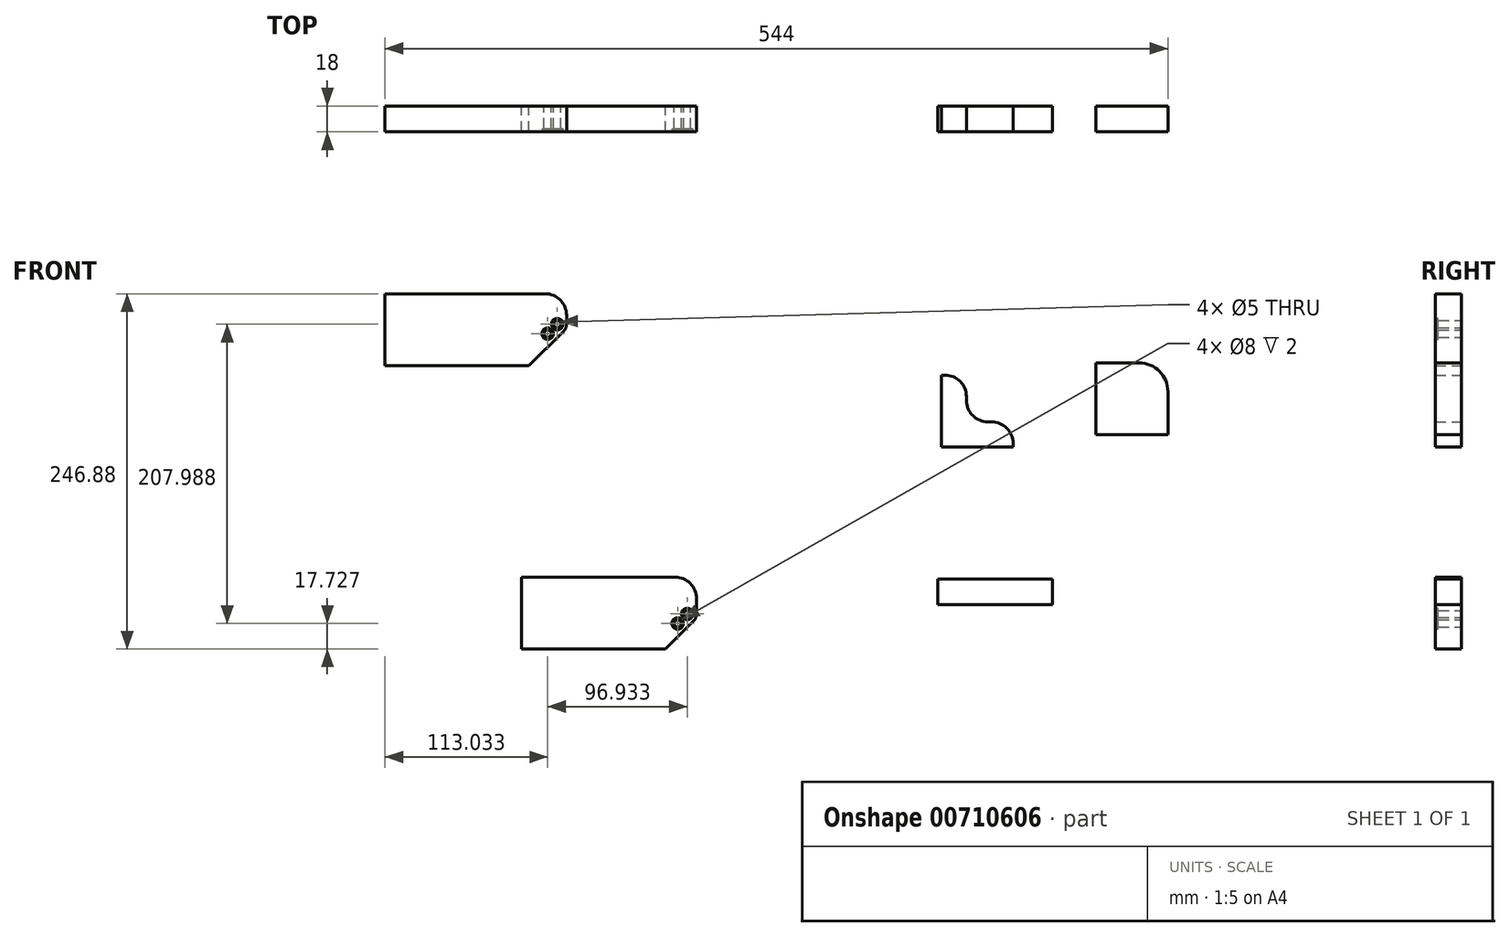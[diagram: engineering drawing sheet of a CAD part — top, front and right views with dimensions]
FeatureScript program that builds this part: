
annotation { "Feature Type Name" : "Feature", "Feature Type Description" : "" }
export const myFeature = defineFeature(function(context is Context, id is Id, definition is map)
    precondition{}
    {
        {
            var Q0;
            Q0=qCreatedBy(makeId("Front.planeOp"),FACE);
            var sketch = newSketch(context, id + "F0", { "sketchPlane" : qUnion([Q0])});
            skLineSegment(sketch, "E0", {"start": v(0, 0) * mm, "end": v(100, 0) * mm});
            skLineSegment(sketch, "E1", {"start": v(100, 0) * mm, "end": v(119.74, 19.74) * mm});
            skLineSegment(sketch, "E2", {"start": v(121.65, 24.34) * mm, "end": v(121.65, 35) * mm});
            skLineSegment(sketch, "E3", {"start": v(106.65, 50) * mm, "end": v(0, 50) * mm});
            skLineSegment(sketch, "E4", {"start": v(0, 50) * mm, "end": v(0, 0) * mm});
            skCircle(sketch, "E5", {"center": v(108.53, 17.73) * mm, "radius": 4 * mm, "construction": true});
            skCircle(sketch, "E6", {"center": v(115.15, 24.34) * mm, "radius": 4 * mm, "construction": true});
            skCircle(sketch, "E7", {"center": v(108.53, 17.73) * mm, "radius": 2.5 * mm});
            skCircle(sketch, "E8", {"center": v(115.15, 24.34) * mm, "radius": 2.5 * mm});
            skLineSegment(sketch, "E9", {"start": v(108.53, 17.73) * mm, "end": v(115.15, 24.34) * mm, "construction": true});
            skLineSegment(sketch, "E10", {"start": v(97.22, 34.7) * mm, "end": v(167.93, -36.01) * mm, "construction": true});
            skLineSegment(sketch, "E11", {"start": v(167.93, -36.01) * mm, "end": v(168.89, -35.06) * mm, "construction": true});
            skLineSegment(sketch, "E12", {"start": v(168.89, -35.06) * mm, "end": v(98.18, 35.65) * mm, "construction": true});
            skLineSegment(sketch, "E13", {"start": v(98.18, 35.65) * mm, "end": v(97.22, 34.7) * mm, "construction": true});
            skLineSegment(sketch, "E14", {"start": v(122.83, 20) * mm, "end": v(122.83, 2) * mm, "construction": true});
            skLineSegment(sketch, "E15", {"start": v(122.83, 2) * mm, "end": v(166.06, 2) * mm, "construction": true});
            skLineSegment(sketch, "E16", {"start": v(166.06, 2) * mm, "end": v(166.06, 20) * mm, "construction": true});
            skLineSegment(sketch, "E17", {"start": v(166.06, 20) * mm, "end": v(122.83, 20) * mm, "construction": true});
            skPoint(sketch, "E18", {"position": v(122.83, 11) * mm});
            skLineSegment(sketch, "E19", {"start": v(143.18, -11.26) * mm, "end": v(144.14, -10.3) * mm, "construction": true});
            skLineSegment(sketch, "E20", {"start": v(0, 0) * mm, "end": v(0, -18) * mm, "construction": true});
            skLineSegment(sketch, "E21", {"start": v(0, -18) * mm, "end": v(233.18, -18) * mm, "construction": true});
            skLineSegment(sketch, "E22", {"start": v(233.18, -18) * mm, "end": v(233.18, 0) * mm, "construction": true});
            skLineSegment(sketch, "E23", {"start": v(233.18, 0) * mm, "end": v(100, 0) * mm, "construction": true});
            skLineSegment(sketch, "E24", {"start": v(289.16, 30.72) * mm, "end": v(344.25, 30.72) * mm});
            skLineSegment(sketch, "E25", {"start": v(344.25, 30.72) * mm, "end": v(344.25, 85.54) * mm});
            skLineSegment(sketch, "E26", {"start": v(344.25, 30.72) * mm, "end": v(298.29, 76.69) * mm});
            skLineSegment(sketch, "E27", {"start": v(289.16, 30.72) * mm, "end": v(289.16, 48.72) * mm});
            skLineSegment(sketch, "E28", {"start": v(289.16, 48.72) * mm, "end": v(369.01, 48.72) * mm});
            skLineSegment(sketch, "E29", {"start": v(369.01, 48.72) * mm, "end": v(369.01, 30.72) * mm});
            skLineSegment(sketch, "E30", {"start": v(369.01, 30.72) * mm, "end": v(344.25, 30.72) * mm});
            skLineSegment(sketch, "E31", {"start": v(-94.82, 196.88) * mm, "end": v(5.18, 196.88) * mm});
            skLineSegment(sketch, "E32", {"start": v(5.18, 196.88) * mm, "end": v(29.42, 221.12) * mm});
            skLineSegment(sketch, "E33", {"start": v(31.32, 225.72) * mm, "end": v(31.32, 231.88) * mm});
            skLineSegment(sketch, "E34", {"start": v(16.32, 246.88) * mm, "end": v(-94.82, 246.88) * mm});
            skLineSegment(sketch, "E35", {"start": v(-94.82, 246.88) * mm, "end": v(-94.82, 196.88) * mm});
            skCircle(sketch, "E36", {"center": v(18.21, 219.1) * mm, "radius": 4 * mm, "construction": true});
            skCircle(sketch, "E37", {"center": v(24.82, 225.72) * mm, "radius": 4 * mm, "construction": true});
            skCircle(sketch, "E38", {"center": v(18.21, 219.1) * mm, "radius": 2.5 * mm});
            skCircle(sketch, "E39", {"center": v(24.82, 225.72) * mm, "radius": 2.5 * mm});
            skLineSegment(sketch, "E40", {"start": v(18.21, 219.1) * mm, "end": v(24.82, 225.72) * mm, "construction": true});
            skLineSegment(sketch, "E41", {"start": v(6.9, 236.07) * mm, "end": v(77.61, 165.36) * mm, "construction": true});
            skLineSegment(sketch, "E42", {"start": v(77.61, 165.36) * mm, "end": v(78.56, 166.32) * mm, "construction": true});
            skLineSegment(sketch, "E43", {"start": v(78.56, 166.32) * mm, "end": v(7.85, 237.03) * mm, "construction": true});
            skLineSegment(sketch, "E44", {"start": v(7.85, 237.03) * mm, "end": v(6.9, 236.07) * mm, "construction": true});
            skLineSegment(sketch, "E45", {"start": v(28, 216.88) * mm, "end": v(28, 198.88) * mm, "construction": true});
            skLineSegment(sketch, "E46", {"start": v(28, 198.88) * mm, "end": v(71.24, 198.88) * mm, "construction": true});
            skLineSegment(sketch, "E47", {"start": v(71.24, 198.88) * mm, "end": v(71.24, 216.88) * mm, "construction": true});
            skLineSegment(sketch, "E48", {"start": v(71.24, 216.88) * mm, "end": v(28, 216.88) * mm, "construction": true});
            skPoint(sketch, "E49", {"position": v(28, 207.88) * mm});
            skLineSegment(sketch, "E50", {"start": v(52.86, 190.11) * mm, "end": v(53.82, 191.07) * mm, "construction": true});
            skLineSegment(sketch, "E51", {"start": v(-94.82, 196.88) * mm, "end": v(-94.82, 178.88) * mm, "construction": true});
            skLineSegment(sketch, "E52", {"start": v(-94.82, 178.88) * mm, "end": v(156.01, 178.88) * mm, "construction": true});
            skLineSegment(sketch, "E53", {"start": v(156.01, 178.88) * mm, "end": v(156.01, 196.88) * mm, "construction": true});
            skLineSegment(sketch, "E54", {"start": v(156.01, 196.88) * mm, "end": v(5.18, 196.88) * mm, "construction": true});
            skPoint(sketch, "E55.visualSharp", {"position": v(31.32, 223.02) * mm});
            skArc(sketch, "E55.filletArc", {"start": v(29.42, 221.12) * mm, "mid": v(30.83, 223.23) * mm, "end": v(31.32, 225.72) * mm});
            skPoint(sketch, "E56.visualSharp", {"position": v(121.65, 21.65) * mm});
            skArc(sketch, "E56.filletArc", {"start": v(119.74, 19.74) * mm, "mid": v(121.15, 21.85) * mm, "end": v(121.65, 24.34) * mm});
            skPoint(sketch, "E57.visualSharp", {"position": v(31.32, 246.88) * mm});
            skArc(sketch, "E57.filletArc", {"start": v(31.32, 231.88) * mm, "mid": v(26.93, 242.48) * mm, "end": v(16.32, 246.88) * mm});
            skPoint(sketch, "E58.visualSharp", {"position": v(121.65, 50) * mm});
            skArc(sketch, "E58.filletArc", {"start": v(121.65, 35) * mm, "mid": v(117.25, 45.6) * mm, "end": v(106.65, 50) * mm});
            skLineSegment(sketch, "E59.bottom", {"start": v(291.67, 140.34) * mm, "end": v(341.67, 140.34) * mm});
            skLineSegment(sketch, "E59.top", {"start": v(291.67, 190.34) * mm, "end": v(294.17, 190.34) * mm});
            skLineSegment(sketch, "E59.left", {"start": v(291.67, 140.34) * mm, "end": v(291.67, 190.34) * mm});
            skLineSegment(sketch, "E59.right", {"start": v(341.67, 140.34) * mm, "end": v(341.67, 142.84) * mm});
            skLineSegment(sketch, "E60.top", {"start": v(326.67, 157.84) * mm, "end": v(324.17, 157.84) * mm});
            skLineSegment(sketch, "E60.right", {"start": v(309.17, 175.34) * mm, "end": v(309.17, 172.84) * mm});
            skPoint(sketch, "E61.visualSharp", {"position": v(309.17, 190.34) * mm});
            skArc(sketch, "E61.filletArc", {"start": v(309.17, 175.34) * mm, "mid": v(304.77, 185.94) * mm, "end": v(294.17, 190.34) * mm});
            skPoint(sketch, "E62.visualSharp", {"position": v(309.17, 157.84) * mm});
            skArc(sketch, "E62.filletArc", {"start": v(309.17, 172.84) * mm, "mid": v(313.56, 162.23) * mm, "end": v(324.17, 157.84) * mm});
            skPoint(sketch, "E63.visualSharp", {"position": v(341.67, 157.84) * mm});
            skArc(sketch, "E63.filletArc", {"start": v(341.67, 142.84) * mm, "mid": v(337.27, 153.44) * mm, "end": v(326.67, 157.84) * mm});
            skLineSegment(sketch, "E64.bottom", {"start": v(399.18, 148.83) * mm, "end": v(449.18, 148.83) * mm});
            skLineSegment(sketch, "E64.top", {"start": v(399.18, 198.83) * mm, "end": v(429.18, 198.83) * mm});
            skLineSegment(sketch, "E64.left", {"start": v(399.18, 148.83) * mm, "end": v(399.18, 198.83) * mm});
            skLineSegment(sketch, "E64.right", {"start": v(449.18, 148.83) * mm, "end": v(449.18, 178.83) * mm});
            skPoint(sketch, "E65.visualSharp", {"position": v(449.18, 198.83) * mm});
            skArc(sketch, "E65.filletArc", {"start": v(449.18, 178.83) * mm, "mid": v(443.32, 192.97) * mm, "end": v(429.18, 198.83) * mm});
            skSolve(sketch);
        }
        {
            var Q0;
            Q0 = qSketchRegion(id + "F0", true);
            extrude(context, id + "F1", {"entities" : qUnion([Q0]), "depth" : 18 * mm, "offsetDistance" : 25 * mm});
        }
        {
            var Q0;
            Q0=makeQuery(id+"F1.opExtrude","CAP_FACE",FACE,{"disambiguationData":[OSD([sQuery(id+"F0.wireOp",EDGE,"E31"),sQuery(id+"F0.wireOp",EDGE,"E32"),sQuery(id+"F0.wireOp",EDGE,"E33"),sQuery(id+"F0.wireOp",EDGE,"E34"),sQuery(id+"F0.wireOp",EDGE,"E35"),sQuery(id+"F0.wireOp",EDGE,"E38"),sQuery(id+"F0.wireOp",EDGE,"E39"),sQuery(id+"F0.wireOp",EDGE,"E55.filletArc"),sQuery(id+"F0.wireOp",EDGE,"E57.filletArc")])],"isStart":false});
            var sketch = newSketch(context, id + "F2", { "sketchPlane" : qUnion([Q0])});
            skCircle(sketch, "E66", {"center": v(18.21, 219.1) * mm, "radius": 4 * mm});
            skCircle(sketch, "E67", {"center": v(24.82, 225.72) * mm, "radius": 4 * mm});
            skCircle(sketch, "E68", {"center": v(115.15, 24.34) * mm, "radius": 4 * mm});
            skCircle(sketch, "E69", {"center": v(108.53, 17.73) * mm, "radius": 4 * mm});
            skSolve(sketch);
        }
        {
            var Q0;
            Q0 = qSketchRegion(id + "F2", true);
            extrude(context, id + "F3", {"entities" : qUnion([Q0]), "operationType" : NewBodyOperationType.REMOVE, "oppositeDirection" : true, "depth" : 2 * mm, "offsetDistance" : 25 * mm});
        }
    });
